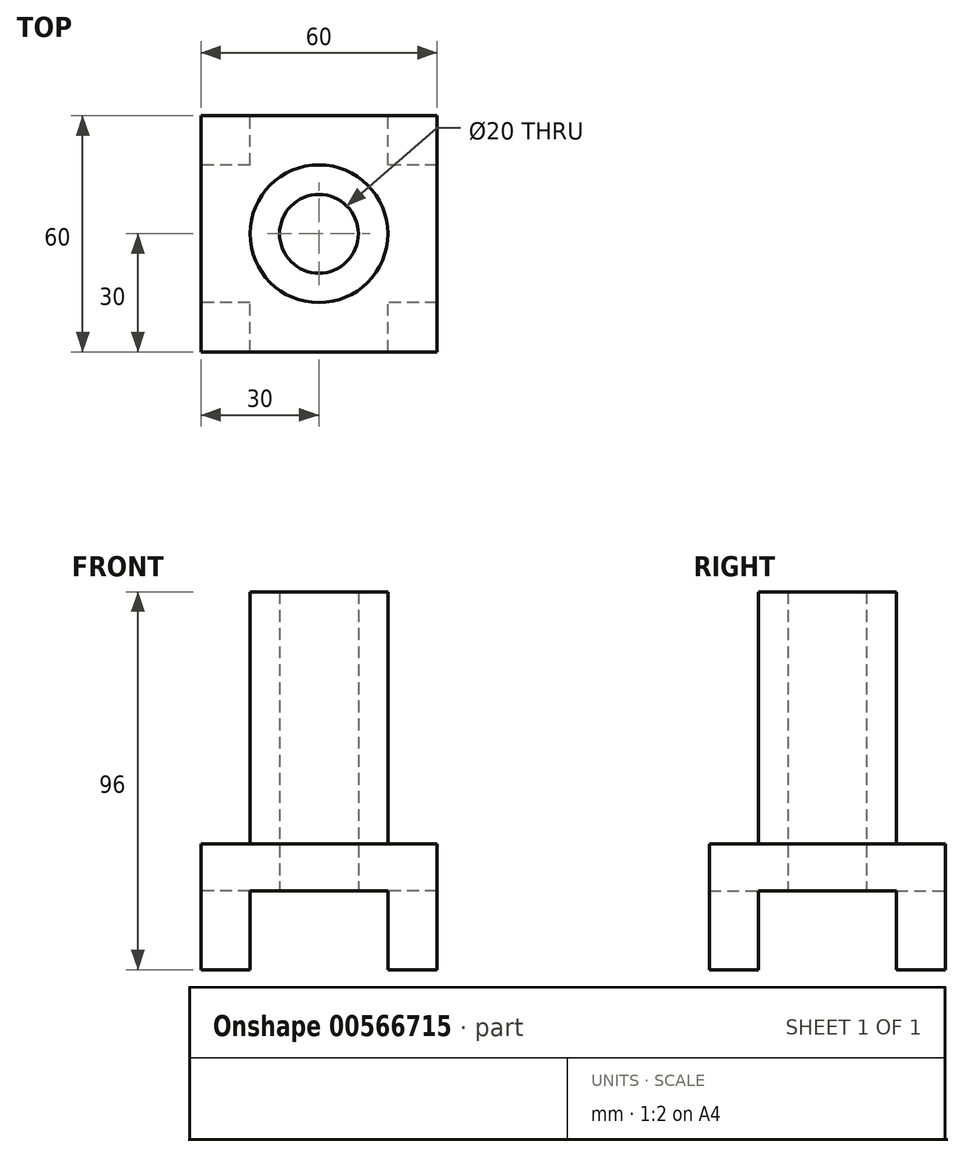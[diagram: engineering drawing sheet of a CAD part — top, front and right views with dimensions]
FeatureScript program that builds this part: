
annotation { "Feature Type Name" : "Feature", "Feature Type Description" : "" }
export const myFeature = defineFeature(function(context is Context, id is Id, definition is map)
    precondition{}
    {
        {
            var Q0;
            Q0=qCreatedBy(makeId("Front.planeOp"),FACE);
            var sketch = newSketch(context, id + "F0", { "sketchPlane" : qUnion([Q0])});
            skLineSegment(sketch, "E0", {"start": v(-30, 0.27) * mm, "end": v(0, 0.27) * mm});
            skLineSegment(sketch, "E1", {"start": v(0, -11.73) * mm, "end": v(-17.5, -11.73) * mm});
            skLineSegment(sketch, "E2", {"start": v(-17.5, -11.73) * mm, "end": v(-17.5, -31.73) * mm});
            skLineSegment(sketch, "E3", {"start": v(-17.5, -31.73) * mm, "end": v(-30, -31.73) * mm});
            skLineSegment(sketch, "E4", {"start": v(-30, -31.73) * mm, "end": v(-30, 0.27) * mm});
            skLineSegment(sketch, "E5", {"start": v(0, 52.66) * mm, "end": v(0, 0.27) * mm, "construction": true});
            skLineSegment(sketch, "E6.MirrorCS", {"start": v(30, -31.73) * mm, "end": v(30, 0.27) * mm});
            skLineSegment(sketch, "E7.MirrorCS", {"start": v(17.5, -31.73) * mm, "end": v(30, -31.73) * mm});
            skLineSegment(sketch, "E8.MirrorCS", {"start": v(17.5, -11.73) * mm, "end": v(17.5, -31.73) * mm});
            skLineSegment(sketch, "E9.MirrorCS", {"start": v(0, -11.73) * mm, "end": v(17.5, -11.73) * mm});
            skLineSegment(sketch, "E10.MirrorCS", {"start": v(30, 0.27) * mm, "end": v(0, 0.27) * mm});
            skSolve(sketch);
        }
        {
            var Q0;
            Q0 = qSketchRegion(id + "F0", true);
            extrude(context, id + "F1", {"entities" : qUnion([Q0]), "endBound" : BoundingType.SYMMETRIC, "depth" : 60 * mm, "offsetDistance" : 25 * mm});
        }
        {
            var Q0;
            Q0=makeQuery(id+"F1.opExtrude","SWEPT_FACE",FACE,{"disambiguationData":[OSD([sQuery(id+"F0.wireOp",EDGE,"E0"),sQuery(id+"F0.wireOp",EDGE,"E10.MirrorCS")])]});
            var sketch = newSketch(context, id + "F2", { "sketchPlane" : qUnion([Q0])});
            skCircle(sketch, "E11", {"center": v(0, 0) * mm, "radius": 17.5 * mm});
            skCircle(sketch, "E12", {"center": v(0, 0) * mm, "radius": 10 * mm});
            skSolve(sketch);
        }
        {
            var Q0;
            Q0 = qSketchRegion(id + "F2", true);
            extrude(context, id + "F3", {"entities" : qUnion([Q0]), "operationType" : NewBodyOperationType.ADD, "depth" : 64 * mm, "offsetDistance" : 25 * mm});
        }
        {
            var Q0;
            Q0=makeQuery(id+"F3.boolean.opBoolean","SPLIT",FACE,{"disambiguationData":[TD([makeQuery(id+"F3.opExtrude","SWEPT_FACE",FACE,{"disambiguationData":[OSD([sQuery(id+"F2.wireOp",EDGE,"E12")])]})])],"derivedFrom":makeQuery(id+"F1.opExtrude","SWEPT_FACE",FACE,{"disambiguationData":[OSD([sQuery(id+"F0.wireOp",EDGE,"E0"),sQuery(id+"F0.wireOp",EDGE,"E10.MirrorCS")])]})});
            extrude(context, id + "F4", {"entities" : qUnion([Q0]), "operationType" : NewBodyOperationType.REMOVE, "endBound" : BoundingType.THROUGH_ALL, "oppositeDirection" : true, "depth" : 25 * mm, "offsetDistance" : 25 * mm});
        }
        {
            var Q0;
            Q0=makeQuery(id+"F1.opExtrude","SWEPT_FACE",FACE,{"disambiguationData":[OSD([sQuery(id+"F0.wireOp",EDGE,"E4")])]});
            var sketch = newSketch(context, id + "F5", { "sketchPlane" : qUnion([Q0])});
            skLineSegment(sketch, "E13.0.1", {"start": v(-17.5, -31.73) * mm, "end": v(17.5, -31.73) * mm});
            skLineSegment(sketch, "E14", {"start": v(-17.5, -31.73) * mm, "end": v(-17.5, -11.73) * mm});
            skLineSegment(sketch, "E15", {"start": v(-17.5, -11.73) * mm, "end": v(17.5, -11.73) * mm});
            skLineSegment(sketch, "E16", {"start": v(17.5, -11.73) * mm, "end": v(17.5, -31.73) * mm});
            skPoint(sketch, "E17.orphan", {"position": v(-30, 0.27) * mm});
            skPoint(sketch, "E13.0.2.end.orphan", {"position": v(30, 0.27) * mm});
            skPoint(sketch, "E18.orphan", {"position": v(30, -31.73) * mm});
            skPoint(sketch, "E19.orphan", {"position": v(-30, -31.73) * mm});
            skPoint(sketch, "E20.orphan", {"position": v(0, 10.79) * mm});
            skSolve(sketch);
        }
        {
            var Q0;
            Q0 = qSketchRegion(id + "F5", true);
            extrude(context, id + "F6", {"entities" : qUnion([Q0]), "operationType" : NewBodyOperationType.REMOVE, "oppositeDirection" : true, "depth" : 93 * mm, "offsetDistance" : 25 * mm});
        }
    });
